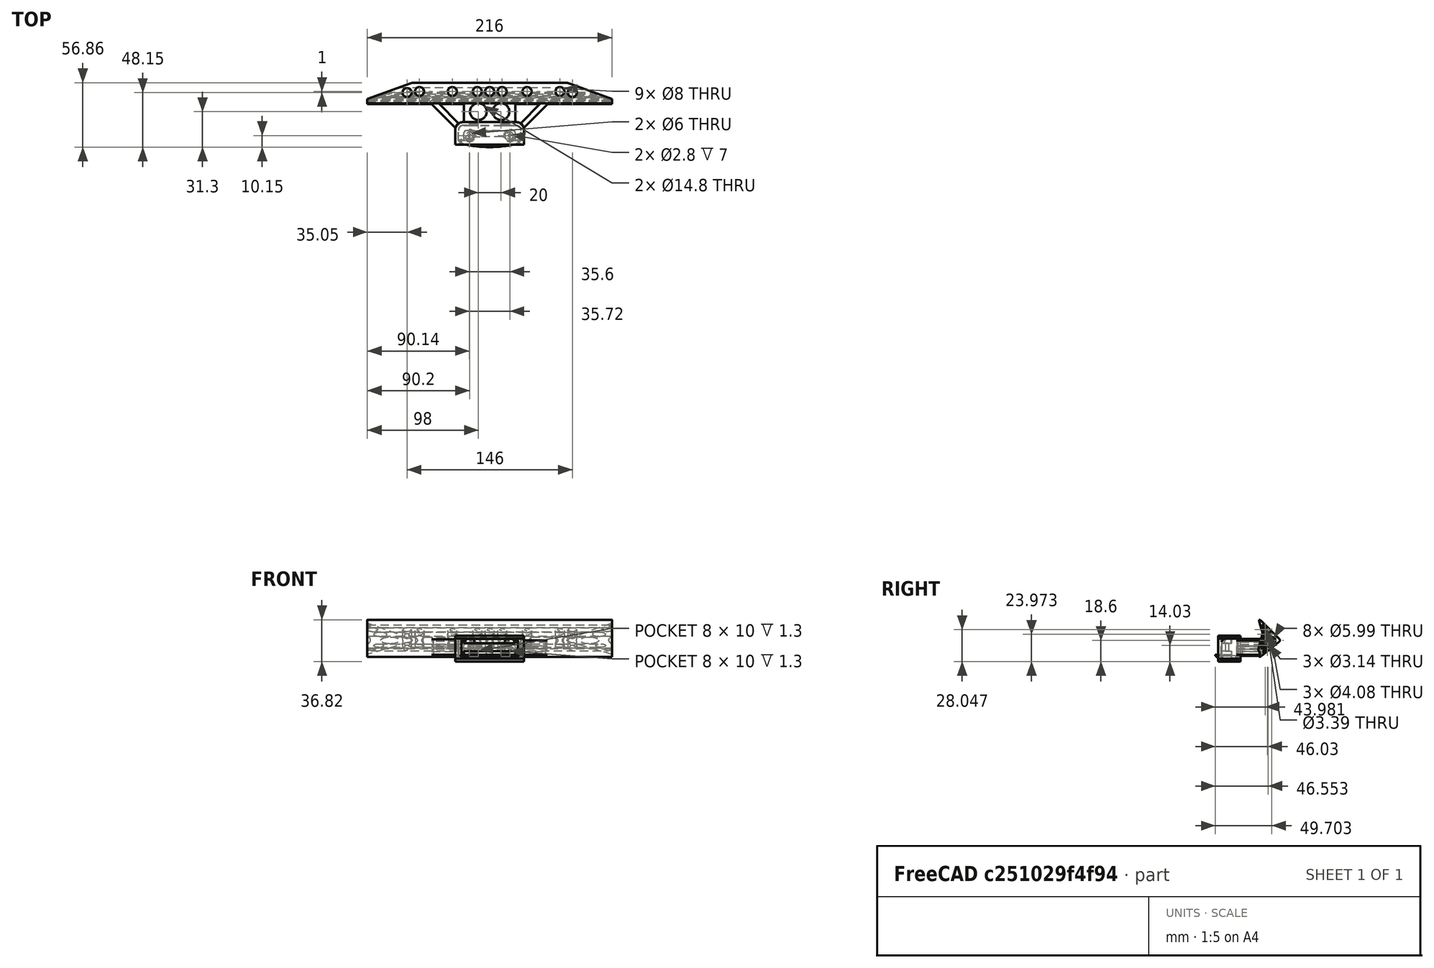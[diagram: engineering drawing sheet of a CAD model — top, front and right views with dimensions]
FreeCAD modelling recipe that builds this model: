
FCSTD DOCUMENT  (FreeCAD 0.21R0.20.1)
Label: 060
License: All rights reserved
LicenseURL: http://en.wikipedia.org/wiki/All_rights_reserved
objects: Part::Cylinder×29, Part::MultiFuse×16, Part::Extrusion×13, Sketcher::SketchObject×12, Part::Box×9, Part::Cut×8, Part::Fillet×8, Part::Chamfer×4
note: 99 computed .brp shape members not serialized (recipe doc carries the construction recipe); baked Part::Feature solids carry a one-line shape summary decoded from their .brp

FEATURE [Sketcher::SketchObject] Sketch  label="attatchmentPiece"
  FullyConstrained = true
  sketch-geometry (20):
    g0: LineSegment StartX=21.05 StartY=0 StartZ=0 EndX=21.05 EndY=-1 EndZ=0
    g1: LineSegment StartX=21.05 StartY=-1 StartZ=0 EndX=21.05 EndY=-4.3 EndZ=0
    g2: LineSegment StartX=-24.15 StartY=4.3 StartZ=0 EndX=21.05 EndY=4.3 EndZ=0
    g3: LineSegment StartX=21.05 StartY=0 StartZ=0 EndX=21.05 EndY=4.3 EndZ=0
    g4-g7: Circle x4 (B-spline internal-alignment scaffolding for g8; pole/knot coordinates omitted)
    g8: BSplineCurve PolesCount=4 KnotsCount=2 Degree=3 IsPeriodic=0
    g9: GeomPoint X=10.05 Y=-1 Z=0
    g10: GeomPoint X=14.55 Y=-4.3 Z=0
    g11: LineSegment StartX=10.05 StartY=-1 StartZ=0 EndX=-10.05 EndY=-1 EndZ=0
    g12: LineSegment StartX=14.55 StartY=-4.3 StartZ=0 EndX=21.05 EndY=-4.3 EndZ=0
    g13: LineSegment StartX=-24.15 StartY=4.3 StartZ=0 EndX=-24.15 EndY=-4.3 EndZ=0
    g14: LineSegment StartX=-13.15 StartY=-1 StartZ=0 EndX=-10.05 EndY=-1 EndZ=0
    g15: LineSegment StartX=-24.15 StartY=-4.3 StartZ=0 EndX=-19.35 EndY=-4.3 EndZ=0
    g16: LineSegment StartX=-19.35 StartY=-4.3 StartZ=0 EndX=-17.65 EndY=-4.3 EndZ=0
    g17: BSplineCurve PolesCount=4 KnotsCount=2 Degree=3 IsPeriodic=0
    g18: Circle CenterX=16.25 CenterY=0 CenterZ=0 NormalX=0 NormalY=0 NormalZ=1 AngleXU=0 Radius=1.4
    g19: Circle CenterX=-19.35 CenterY=0 CenterZ=0 NormalX=0 NormalY=0 NormalZ=1 AngleXU=0 Radius=1.4
  constraints (41):
    c: Vertical(g0)
    c: Coincident(g1,g0)
    c: Vertical(g1)
    c: Block(g0)
    c: Horizontal(g2)
    c: Vertical(g3)
    c: Coincident(g3,g2)
    c: Block(g2)
    c: Block(g3)
    c: Weight(g4) = 1
    c: Equal(g4,g5)
    c: Equal(g4,g6)
    c: Equal(g4,g7)
    c: InternalAlignment(g4-g7 -> g8) x4
    c: InternalAlignment(g9,g8)
    c: InternalAlignment(g10,g8)
    c: Block(g8)
    c: Coincident(g11,g8)
    c: Horizontal(g11)
    c: Coincident(g12,g8)
    c: Coincident(g12,g1)
    c: Horizontal(g12)
    c: Distance(g2) = 45.2
    c: Coincident(g13,g2)
    c: Vertical(g13)
    c: Horizontal(g14)
    c: Distance(g14) = 3.1
    c: Horizontal(g15)
    c: Block(g17)
    c: Coincident(g16,g15)
    c: Coincident(g16,g17)
    c: Horizontal(g16)
    c: Block(g16)
    c: Coincident(g17,g14)
    c: Block(g15)
    c: Block(g11)
    c: Block(g13)
    c: Distance(g15) = 4.8
    c: Distance(g16) = 1.7
    c: Block(g18)
    c: Block(g19)
FEATURE [Part::Extrusion] Extrude  label="attatchmentPiece001"
  Base = -> Sketch
  Dir = (0,0,1)
  DirMode = 2
  FaceMakerClass = Part::FaceMakerBullseye
  LengthFwd = 7
  LengthRev = 0
  Solid = true
  Symmetric = false
FEATURE [Sketcher::SketchObject] Sketch001  label="attatchmentPieceSurround"
  FullyConstrained = true
  sketch-geometry (18):
    g0: LineSegment StartX=25.85 StartY=-4.3 StartZ=0 EndX=21.05 EndY=-4.3 EndZ=0
    g1: LineSegment StartX=25.85 StartY=-4.3 StartZ=0 EndX=25.85 EndY=4.3 EndZ=0
    g2: LineSegment StartX=-21.05 StartY=8.9 StartZ=0 EndX=21.05 EndY=8.9 EndZ=0
    g3: Circle CenterX=21.05 CenterY=8.9 CenterZ=0 NormalX=0 NormalY=0 NormalZ=1 AngleXU=0 Radius=1
    g4: Circle CenterX=25.85 CenterY=8.9 CenterZ=0 NormalX=0 NormalY=0 NormalZ=1 AngleXU=0 Radius=1
    g5: Circle CenterX=25.85 CenterY=4.3 CenterZ=0 NormalX=0 NormalY=0 NormalZ=1 AngleXU=0 Radius=1
    g6: BSplineCurve PolesCount=3 KnotsCount=2 Degree=2 IsPeriodic=0
    g7: GeomPoint X=21.05 Y=8.9 Z=0
    g8: GeomPoint X=25.85 Y=4.3 Z=0
    g9: ArcOfCircle CenterX=19.45 CenterY=2.7 CenterZ=0 NormalX=0 NormalY=0 NormalZ=1 AngleXU=0 Radius=1.6 StartAngle=0 EndAngle=1.5708
    g10: LineSegment StartX=21.05 StartY=2.7 StartZ=0 EndX=21.05 EndY=-4.3 EndZ=0
    g11: BSplineCurve PolesCount=3 KnotsCount=2 Degree=2 IsPeriodic=0
    g12: LineSegment StartX=-28.95 StartY=-4.3 StartZ=0 EndX=-28.95 EndY=4.3 EndZ=0
    g13: LineSegment StartX=-24.15 StartY=-4.3 StartZ=0 EndX=-28.95 EndY=-4.3 EndZ=0
    g14: LineSegment StartX=-24.15 StartY=2.7 StartZ=0 EndX=-24.15 EndY=-4.3 EndZ=0
    g15: ArcOfCircle CenterX=-22.55 CenterY=2.7 CenterZ=0 NormalX=0 NormalY=0 NormalZ=1 AngleXU=0 Radius=1.6 StartAngle=1.5708 EndAngle=3.14159
    g16: LineSegment StartX=-24.15 StartY=8.9 StartZ=0 EndX=-21.05 EndY=8.9 EndZ=0
    g17: LineSegment StartX=-22.55 StartY=4.3 StartZ=0 EndX=19.45 EndY=4.3 EndZ=0
  constraints (38):
    c: Horizontal(g0)
    c: Vertical(g1)
    c: Coincident(g1,g0)
    c: Horizontal(g2)
    c: Distance(g2) = 42.1
    c: Block(g2)
    c: Coincident(g6,g2)
    c: Weight(g3) = 1
    c: Equal(g3,g4)
    c: Equal(g3,g5)
    c: Coincident(g6,g1)
    c: InternalAlignment(g3,g6)
    c: InternalAlignment(g4,g6)
    c: InternalAlignment(g5,g6)
    c: InternalAlignment(g7,g6)
    c: InternalAlignment(g8,g6)
    c: Block(g0)
    c: Block(g6)
    c: Block(g9)
    c: Coincident(g10,g9)
    c: Coincident(g10,g0)
    c: Vertical(g10)
    c: Horizontal(g13)
    c: Coincident(g12,g13)
    c: Vertical(g12)
    c: Coincident(g11,g12)
    c: Block(g12)
    c: Block(g11)
    c: Block(g15)
    c: Coincident(g14,g15)
    c: Coincident(g14,g13)
    c: Vertical(g14)
    c: Coincident(g16,g11)
    c: Coincident(g16,g2)
    c: Horizontal(g16)
    c: Coincident(g17,g15)
    c: Coincident(g17,g9)
    c: Horizontal(g17)
FEATURE [Part::Extrusion] Extrude001  label="attatchmentPieceSurround001"
  Base = -> Sketch001
  Dir = (0,0,1)
  DirMode = 2
  FaceMakerClass = Part::FaceMakerBullseye
  LengthFwd = 14.7
  LengthRev = 0
  Placement = pos=(0,0,-4.1) rot=(0,0,1;0rad)
  Solid = true
  Symmetric = false
FEATURE [Sketcher::SketchObject] Sketch002  label="attatchmentPieceEndScrewHoleCaps"
  FullyConstrained = true
  sketch-geometry (10):
    g0: ArcOfCircle CenterX=16.25 CenterY=0 CenterZ=0 NormalX=0 NormalY=0 NormalZ=1 AngleXU=0 Radius=4.3 StartAngle=2.05456 EndAngle=5.79942
    g1: LineSegment StartX=14.25 StartY=3.80657 StartZ=0 EndX=14.25 EndY=6 EndZ=0
    g2: LineSegment StartX=20.0566 StartY=-2 StartZ=0 EndX=22.25 EndY=-2 EndZ=0
    g3: LineSegment StartX=22.25 StartY=-2 StartZ=0 EndX=22.25 EndY=6 EndZ=0
    g4: LineSegment StartX=14.25 StartY=6 StartZ=0 EndX=22.25 EndY=6 EndZ=0
    g5: LineSegment StartX=-25.35 StartY=-2 StartZ=0 EndX=-25.35 EndY=6 EndZ=0
    g6: LineSegment StartX=-25.35 StartY=-2 StartZ=0 EndX=-23.1566 EndY=-2 EndZ=0
    g7: LineSegment StartX=-17.35 StartY=6 StartZ=0 EndX=-25.35 EndY=6 EndZ=0
    g8: LineSegment StartX=-17.35 StartY=3.80657 StartZ=0 EndX=-17.35 EndY=6 EndZ=0
    g9: ArcOfCircle CenterX=-19.35 CenterY=0 CenterZ=0 NormalX=0 NormalY=0 NormalZ=1 AngleXU=0 Radius=4.3 StartAngle=3.62536 EndAngle=7.37022
  constraints (25):
    c: Block(g0)
    c: Vertical(g1)
    c: Horizontal(g2)
    c: Coincident(g3,g2)
    c: Vertical(g3)
    c: Coincident(g4,g1)
    c: Horizontal(g4)
    c: Coincident(g3,g4)
    c: Block(g4)
    c: Block(g3)
    c: Coincident(g0,g1)
    c: Coincident(g0,g2)
    c: Block(g1)
    c: Block(g9)
    c: Horizontal(g6)
    c: Vertical(g8)
    c: Coincident(g7,g8)
    c: Horizontal(g7)
    c: Coincident(g5,g6)
    c: Vertical(g5)
    c: Coincident(g5,g7)
    c: Block(g7)
    c: Block(g5)
    c: Coincident(g9,g6)
    c: Coincident(g9,g8)
FEATURE [Part::Extrusion] Extrude002  label="attatchmentPieceEndScrewHoleCaps001"
  Base = -> Sketch002
  Dir = (0,0,1)
  DirMode = 2
  FaceMakerClass = Part::FaceMakerBullseye
  LengthFwd = 3.6
  LengthRev = 0
  Placement = pos=(0,0,7) rot=(0,0,1;0rad)
  Solid = true
  Symmetric = false
FEATURE [Sketcher::SketchObject] Sketch003  label="mainBumpperPieceAttatchment"
  FullyConstrained = true
  sketch-geometry (42):
    g0: Circle CenterX=28.85 CenterY=4.3 CenterZ=0 NormalX=0 NormalY=0 NormalZ=1 AngleXU=0 Radius=1
    g1: Circle CenterX=28.85 CenterY=11.9 CenterZ=0 NormalX=0 NormalY=0 NormalZ=1 AngleXU=0 Radius=1
    g2: Circle CenterX=21.05 CenterY=11.9 CenterZ=0 NormalX=0 NormalY=0 NormalZ=1 AngleXU=0 Radius=1
    g3: BSplineCurve PolesCount=3 KnotsCount=2 Degree=2 IsPeriodic=0
    g4: GeomPoint X=28.85 Y=4.3 Z=0
    g5: GeomPoint X=21.05 Y=11.9 Z=0
    g6: LineSegment StartX=-21.05 StartY=11.9 StartZ=0 EndX=21.05 EndY=11.9 EndZ=0
    g7: LineSegment StartX=28.85 StartY=4.3 StartZ=0 EndX=28.85 EndY=-4.3 EndZ=0
    g8: Circle CenterX=21.05 CenterY=9.2 CenterZ=0 NormalX=0 NormalY=0 NormalZ=1 AngleXU=0 Radius=1
    g9: Circle CenterX=26.15 CenterY=9.2 CenterZ=0 NormalX=0 NormalY=0 NormalZ=1 AngleXU=0 Radius=1
    g10: Circle CenterX=26.15 CenterY=4.3 CenterZ=0 NormalX=0 NormalY=0 NormalZ=1 AngleXU=0 Radius=1
    g11: BSplineCurve PolesCount=3 KnotsCount=2 Degree=2 IsPeriodic=0
    g12: GeomPoint X=21.05 Y=9.2 Z=0
    g13: GeomPoint X=26.15 Y=4.3 Z=0
    g14: LineSegment StartX=-21.05 StartY=9.2 StartZ=0 EndX=21.05 EndY=9.2 EndZ=0
    g15: LineSegment StartX=26.15 StartY=-4.3 StartZ=0 EndX=26.15 EndY=4.3 EndZ=0
    g16: LineSegment StartX=26.15 StartY=-4.3 StartZ=0 EndX=26.15 EndY=-4.6 EndZ=0
    g17: LineSegment StartX=23.45 StartY=-4.6 StartZ=0 EndX=26.15 EndY=-4.6 EndZ=0
    g18: LineSegment StartX=28.85 StartY=-4.3 StartZ=0 EndX=28.85 EndY=-7.9 EndZ=0
    g19: LineSegment StartX=23.45 StartY=-4.6 StartZ=0 EndX=23.45 EndY=-5.3 EndZ=0
    g20: Circle CenterX=28.85 CenterY=-7.9 CenterZ=0 NormalX=0 NormalY=0 NormalZ=1 AngleXU=0 Radius=1
    g21: Circle CenterX=26.15 CenterY=-8.2 CenterZ=0 NormalX=0 NormalY=0 NormalZ=1 AngleXU=0 Radius=1
    g22: Circle CenterX=23.45 CenterY=-5.3 CenterZ=0 NormalX=0 NormalY=0 NormalZ=1 AngleXU=0 Radius=1
    g23: BSplineCurve PolesCount=3 KnotsCount=2 Degree=2 IsPeriodic=0
    g24: GeomPoint X=28.85 Y=-7.9 Z=0
    g25: GeomPoint X=23.45 Y=-5.3 Z=0
    g26: LineSegment StartX=-21.05 StartY=9.2 StartZ=0 EndX=-24.15 EndY=9.2 EndZ=0
    g27: BSplineCurve PolesCount=3 KnotsCount=2 Degree=2 IsPeriodic=0
    g28: LineSegment StartX=-29.25 StartY=-4.3 StartZ=0 EndX=-29.25 EndY=-4.6 EndZ=0
    g29: LineSegment StartX=-29.25 StartY=-4.6 StartZ=0 EndX=-26.55 EndY=-4.6 EndZ=0
    g30: LineSegment StartX=-31.95 StartY=-4.3 StartZ=0 EndX=-31.95 EndY=-7.9 EndZ=0
    g31: LineSegment StartX=-26.55 StartY=-4.6 StartZ=0 EndX=-26.55 EndY=-5.3 EndZ=0
    g32: Circle CenterX=-31.95 CenterY=-7.9 CenterZ=0 NormalX=0 NormalY=0 NormalZ=1 AngleXU=0 Radius=1
    g33: Circle CenterX=-29.25 CenterY=-8.2 CenterZ=0 NormalX=0 NormalY=0 NormalZ=1 AngleXU=0 Radius=1
    g34: Circle CenterX=-26.55 CenterY=-5.3 CenterZ=0 NormalX=0 NormalY=0 NormalZ=1 AngleXU=0 Radius=1
    g35: BSplineCurve PolesCount=3 KnotsCount=2 Degree=2 IsPeriodic=0
    g36: GeomPoint X=-31.95 Y=-7.9 Z=0
    g37: GeomPoint X=-26.55 Y=-5.3 Z=0
    g38: LineSegment StartX=-31.95 StartY=4.3 StartZ=0 EndX=-31.95 EndY=-4.3 EndZ=0
    g39: LineSegment StartX=-29.25 StartY=-4.3 StartZ=0 EndX=-29.25 EndY=4.3 EndZ=0
    g40: BSplineCurve PolesCount=3 KnotsCount=2 Degree=2 IsPeriodic=0
    g41: LineSegment StartX=-21.05 StartY=11.9 StartZ=0 EndX=-24.15 EndY=11.9 EndZ=0
  constraints (78):
    c: Weight(g0) = 1
    c: Equal(g0,g1)
    c: Equal(g0,g2)
    c: InternalAlignment(g0,g3)
    c: InternalAlignment(g1,g3)
    c: InternalAlignment(g2,g3)
    c: InternalAlignment(g4,g3)
    c: InternalAlignment(g5,g3)
    c: Block(g3)
    c: Horizontal(g6)
    c: Vertical(g7)
    c: Block(g7)
    c: Block(g6)
    c: Weight(g8) = 1
    c: Equal(g8,g9)
    c: Equal(g8,g10)
    c: InternalAlignment(g8,g11)
    c: InternalAlignment(g9,g11)
    c: InternalAlignment(g10,g11)
    c: InternalAlignment(g12,g11)
    c: InternalAlignment(g13,g11)
    c: Horizontal(g14)
    c: Vertical(g15)
    c: Block(g11)
    c: Block(g15)
    c: Block(g14)
    c: Coincident(g16,g15)
    c: Vertical(g16)
    c: Distance(g16) = 0.3
    c: Horizontal(g17)
    c: Coincident(g17,g16)
    c: Coincident(g18,g7)
    c: Vertical(g18)
    c: Distance(g18) = 3.6
    c: Vertical(g19)
    c: Coincident(g19,g17)
    c: Coincident(g23,g18)
    c: Weight(g20) = 1
    c: Equal(g20,g21)
    c: Equal(g20,g22)
    c: Coincident(g23,g19)
    c: InternalAlignment(g20,g23)
    c: InternalAlignment(g21,g23)
    c: InternalAlignment(g22,g23)
    c: InternalAlignment(g24,g23)
    c: InternalAlignment(g25,g23)
    c: Block(g23)
    c: Horizontal(g26)
    c: Distance(g26) = 3.1
    c: Block(g27)
    c: Vertical(g38)
    c: Block(g38)
    c: Vertical(g39)
    c: Block(g40)
    c: Block(g39)
    c: Vertical(g28)
    c: Coincident(g28,g39)
    c: Coincident(g29,g28)
    c: Horizontal(g29)
    c: Vertical(g30)
    c: Coincident(g30,g38)
    c: Coincident(g31,g29)
    c: Vertical(g31)
    c: Coincident(g35,g30)
    c: Equal(g32,g33)
    c: Equal(g32,g34)
    c: Coincident(g35,g31)
    c: InternalAlignment(g32,g35)
    c: InternalAlignment(g33,g35)
    c: InternalAlignment(g34,g35)
    c: InternalAlignment(g36,g35)
    c: InternalAlignment(g37,g35)
    c: Block(g35)
    c: Coincident(g40,g26)
    c: Block(g29)
    c: Horizontal(g41)
    c: Equal(g26,g41) = 3.1
    c: Coincident(g41,g6)
FEATURE [Part::Box] Box  label="bumpperExtension"
  AttacherType = Attacher::AttachEngine3D
  Height = 14.7
  Length = 45.2
  Placement = pos=(-24.15,11.9,-4.1) rot=(0,0,1;0rad)
  Width = 18
FEATURE [Sketcher::SketchObject] Sketch004  label="bumpperMain"
  FullyConstrained = true
  Placement = pos=(0,0,0) rot=(0.57735,0.57735,0.57735;2.0944rad)
  sketch-geometry (62):
    g0: Circle CenterX=-3.12329 CenterY=2.49901 CenterZ=0 NormalX=0 NormalY=0 NormalZ=1 AngleXU=0 Radius=1
    g1: Circle CenterX=0 CenterY=0 CenterZ=0 NormalX=0 NormalY=0 NormalZ=1 AngleXU=0 Radius=1
    g2: Circle CenterX=-1.35243 CenterY=3.60648 CenterZ=0 NormalX=0 NormalY=0 NormalZ=1 AngleXU=0 Radius=1
    g3: BSplineCurve PolesCount=3 KnotsCount=2 Degree=2 IsPeriodic=0
    g4: GeomPoint X=-3.12329 Y=2.49901 Z=0
    g5: GeomPoint X=-1.35243 Y=3.60648 Z=0
    g6: Circle CenterX=-2.83953 CenterY=33.0261 CenterZ=0 NormalX=0 NormalY=0 NormalZ=1 AngleXU=0 Radius=1
    g7: Circle CenterX=0 CenterY=35.8434 CenterZ=0 NormalX=0 NormalY=0 NormalZ=1 AngleXU=0 Radius=1
    g8: Circle CenterX=-1.15771 CenterY=32.0146 CenterZ=0 NormalX=0 NormalY=0 NormalZ=1 AngleXU=0 Radius=1
    g9: BSplineCurve PolesCount=3 KnotsCount=2 Degree=2 IsPeriodic=0
    g10: GeomPoint X=-2.83953 Y=33.0261 Z=0
    g11: GeomPoint X=-1.15771 Y=32.0146 Z=0
    g12: Circle CenterX=-18.2963 CenterY=17.6904 CenterZ=0 NormalX=0 NormalY=0 NormalZ=1 AngleXU=0 Radius=1
    g13: Circle CenterX=-20 CenterY=16 CenterZ=0 NormalX=0 NormalY=0 NormalZ=1 AngleXU=0 Radius=1
    g14: Circle CenterX=-18.1259 CenterY=14.5008 CenterZ=0 NormalX=0 NormalY=0 NormalZ=1 AngleXU=0 Radius=1
    g15: BSplineCurve PolesCount=3 KnotsCount=2 Degree=2 IsPeriodic=0
    g16: GeomPoint X=-18.2963 Y=17.6904 Z=0
    g17: GeomPoint X=-18.1259 Y=14.5008 Z=0
    g18: LineSegment StartX=-18.2963 StartY=17.6904 StartZ=0 EndX=-2.83953 EndY=33.0261 EndZ=0
    g19: LineSegment StartX=-18.1259 StartY=14.5008 StartZ=0 EndX=-3.12329 EndY=2.49901 EndZ=0
    g20: Circle CenterX=-11.9527 CenterY=16 CenterZ=0 NormalX=0 NormalY=0 NormalZ=1 AngleXU=0 Radius=2.99582
    g21: Circle CenterX=-8.803 CenterY=21.3731 CenterZ=0 NormalX=0 NormalY=0 NormalZ=1 AngleXU=0 Radius=2.03939
    g22: Circle CenterX=-6.23123 CenterY=25.4475 CenterZ=0 NormalX=0 NormalY=0 NormalZ=1 AngleXU=0 Radius=1.69309
    g23: Circle CenterX=-4.38186 CenterY=28.6261 CenterZ=0 NormalX=0 NormalY=0 NormalZ=1 AngleXU=0 Radius=1.13029
    g24: Circle CenterX=-8.28033 CenterY=11.4296 CenterZ=0 NormalX=0 NormalY=0 NormalZ=1 AngleXU=0 Radius=1.57213
    g25: Circle CenterX=-5.93972 CenterY=8.22213 CenterZ=0 NormalX=0 NormalY=0 NormalZ=1 AngleXU=0 Radius=1.28743
    g26: Circle CenterX=-3.47023 CenterY=24.3665 CenterZ=0 NormalX=0 NormalY=0 NormalZ=1 AngleXU=0 Radius=1
    g27: Circle CenterX=-3.90437 CenterY=22.9307 CenterZ=0 NormalX=0 NormalY=0 NormalZ=1 AngleXU=0 Radius=1
    g28: Circle CenterX=-3.53772 CenterY=21.4762 CenterZ=0 NormalX=0 NormalY=0 NormalZ=1 AngleXU=0 Radius=1
    g29: BSplineCurve PolesCount=3 KnotsCount=2 Degree=2 IsPeriodic=0
    g30: GeomPoint X=-3.47023 Y=24.3665 Z=0
    g31: GeomPoint X=-3.53772 Y=21.4762 Z=0
    g32: LineSegment StartX=-1.15771 StartY=32.0146 StartZ=0 EndX=-3.47023 EndY=24.3665 EndZ=0
    g33: Circle CenterX=-5.41867 CenterY=17.9226 CenterZ=0 NormalX=0 NormalY=0 NormalZ=1 AngleXU=0 Radius=1
    g34: Circle CenterX=-6 CenterY=16 CenterZ=0 NormalX=0 NormalY=0 NormalZ=1 AngleXU=0 Radius=1
    g35: Circle CenterX=-5.22753 CenterY=13.9401 CenterZ=0 NormalX=0 NormalY=0 NormalZ=1 AngleXU=0 Radius=1
    g36: BSplineCurve PolesCount=3 KnotsCount=2 Degree=2 IsPeriodic=0
    g37: GeomPoint X=-5.41867 Y=17.9226 Z=0
    g38: GeomPoint X=-5.22753 Y=13.9401 Z=0
    g39: Circle CenterX=-3.98946 CenterY=10.6386 CenterZ=0 NormalX=0 NormalY=0 NormalZ=1 AngleXU=0 Radius=1
    g40: Circle CenterX=-2.58497 CenterY=6.89324 CenterZ=0 NormalX=0 NormalY=0 NormalZ=1 AngleXU=0 Radius=1
    g41: Circle CenterX=-3.11001 CenterY=10.8586 CenterZ=0 NormalX=0 NormalY=0 NormalZ=1 AngleXU=0 Radius=1
    g42: BSplineCurve PolesCount=3 KnotsCount=2 Degree=2 IsPeriodic=0
    g43: GeomPoint X=-3.98946 Y=10.6386 Z=0
    g44: GeomPoint X=-3.11001 Y=10.8586 Z=0
    g45: Circle CenterX=-1.35243 CenterY=3.60648 CenterZ=0 NormalX=0 NormalY=0 NormalZ=1 AngleXU=0 Radius=1
    g46: Circle CenterX=-1.76142 CenterY=4.69712 CenterZ=0 NormalX=0 NormalY=0 NormalZ=1 AngleXU=0 Radius=1
    g47: Circle CenterX=-1.05937 CenterY=5.79125 CenterZ=0 NormalX=0 NormalY=0 NormalZ=1 AngleXU=0 Radius=1
    g48: BSplineCurve PolesCount=3 KnotsCount=2 Degree=2 IsPeriodic=0
    g49: GeomPoint X=-1.35243 Y=3.60648 Z=0
    g50: GeomPoint X=-1.05937 Y=5.79125 Z=0
    g51: Circle CenterX=-0.519336 CenterY=6.6329 CenterZ=0 NormalX=0 NormalY=0 NormalZ=1 AngleXU=0 Radius=1
    g52: Circle CenterX=0 CenterY=7.44228 CenterZ=0 NormalX=0 NormalY=0 NormalZ=1 AngleXU=0 Radius=1
    g53: Circle CenterX=-0.244436 CenterY=8.41194 CenterZ=0 NormalX=0 NormalY=0 NormalZ=1 AngleXU=0 Radius=1
    g54: BSplineCurve PolesCount=3 KnotsCount=2 Degree=2 IsPeriodic=0
    g55: GeomPoint X=-0.519336 Y=6.6329 Z=0
    g56: GeomPoint X=-0.244436 Y=8.41194 Z=0
    g57: LineSegment StartX=-3.53772 StartY=21.4762 StartZ=0 EndX=-0.244436 EndY=8.41194 EndZ=0
    g58: LineSegment StartX=-5.22753 StartY=13.9401 StartZ=0 EndX=-3.98946 EndY=10.6386 EndZ=0
    g59: LineSegment StartX=-1.05937 StartY=5.79125 StartZ=0 EndX=-0.519336 EndY=6.6329 EndZ=0
    g60: BSplineCurve PolesCount=3 KnotsCount=2 Degree=2 IsPeriodic=0
    g61: LineSegment StartX=-4.0304 StartY=17.8099 StartZ=0 EndX=-3.11001 EndY=10.8586 EndZ=0
  constraints (96):
    c: Weight(g0) = 1
    c: Equal(g0,g1)
    c: Equal(g0,g2)
    c: InternalAlignment(g0,g3)
    c: InternalAlignment(g1,g3)
    c: InternalAlignment(g2,g3)
    c: InternalAlignment(g4,g3)
    c: InternalAlignment(g5,g3)
    c: Block(g3)
    c: Weight(g6) = 1
    c: Equal(g6,g7)
    c: Equal(g6,g8)
    c: InternalAlignment(g6,g9)
    c: InternalAlignment(g7,g9)
    c: InternalAlignment(g8,g9)
    c: InternalAlignment(g10,g9)
    c: InternalAlignment(g11,g9)
    c: Block(g9)
    c: Weight(g12) = 1
    c: Equal(g12,g13)
    c: Equal(g12,g14)
    c: InternalAlignment(g12,g15)
    c: InternalAlignment(g13,g15)
    c: InternalAlignment(g14,g15)
    c: InternalAlignment(g16,g15)
    c: InternalAlignment(g17,g15)
    c: Block(g15)
    c: Coincident(g18,g15)
    c: Coincident(g18,g9)
    c: Coincident(g19,g15)
    c: Coincident(g19,g3)
    c: Block(g25)
    c: Block(g24)
    c: Block(g20)
    c: Block(g21)
    c: Block(g22)
    c: Block(g23)
    c: Weight(g26) = 1
    c: Equal(g26,g27)
    c: Equal(g26,g28)
    c: InternalAlignment(g26,g29)
    c: InternalAlignment(g27,g29)
    c: InternalAlignment(g28,g29)
    c: InternalAlignment(g30,g29)
    c: InternalAlignment(g31,g29)
    c: Block(g29)
    c: Coincident(g32,g9)
    c: Coincident(g32,g29)
    c: Weight(g33) = 1
    c: Equal(g33,g34)
    c: Equal(g33,g35)
    c: InternalAlignment(g33,g36)
    c: InternalAlignment(g34,g36)
    c: InternalAlignment(g35,g36)
    c: InternalAlignment(g37,g36)
    c: InternalAlignment(g38,g36)
    c: Block(g36)
    c: Weight(g39) = 1
    c: Equal(g39,g40)
    c: Equal(g39,g41)
    c: InternalAlignment(g39,g42)
    c: InternalAlignment(g40,g42)
    c: InternalAlignment(g41,g42)
    c: InternalAlignment(g43,g42)
    c: InternalAlignment(g44,g42)
    c: Block(g42)
    c: Coincident(g48,g3)
    c: Weight(g45) = 1
    c: Equal(g45,g46)
    c: Equal(g45,g47)
    c: InternalAlignment(g45,g48)
    c: InternalAlignment(g46,g48)
    c: InternalAlignment(g47,g48)
    c: InternalAlignment(g49,g48)
    c: InternalAlignment(g50,g48)
    c: Block(g48)
    c: Weight(g51) = 1
    c: Equal(g51,g52)
    c: Equal(g51,g53)
    c: InternalAlignment(g51,g54)
    c: InternalAlignment(g52,g54)
    c: InternalAlignment(g53,g54)
    c: InternalAlignment(g55,g54)
    c: InternalAlignment(g56,g54)
    c: Block(g54)
    c: Coincident(g57,g29)
    c: Coincident(g57,g54)
    c: Block(g57)
    c: Coincident(g58,g36)
    c: Coincident(g58,g42)
    c: Coincident(g59,g48)
    c: Coincident(g59,g54)
    c: Block(g60)
    c: Coincident(g60,g36)
    c: Coincident(g61,g60)
    c: Coincident(g61,g42)
FEATURE [Part::Extrusion] Extrude004  label="bumpperMain001"
  Base = -> Sketch004
  Dir = (1,0,0)
  DirMode = 2
  FaceMakerClass = Part::FaceMakerBullseye
  LengthFwd = 216
  LengthRev = 0
  Placement = pos=(106.45,27.6,-6.6) rot=(0,0,1;3.14159rad)
  Solid = true
  Symmetric = false
FEATURE [Sketcher::SketchObject] Sketch005  label="attatchmentPieceBottom"
  FullyConstrained = true
  sketch-geometry (20):
    g0: LineSegment StartX=25.85 StartY=-4.3 StartZ=0 EndX=25.85 EndY=4.3 EndZ=0
    g1: LineSegment StartX=-21.05 StartY=8.9 StartZ=0 EndX=21.05 EndY=8.9 EndZ=0
    g2: Circle CenterX=21.05 CenterY=8.9 CenterZ=0 NormalX=0 NormalY=0 NormalZ=1 AngleXU=0 Radius=1
    g3: Circle CenterX=25.85 CenterY=8.9 CenterZ=0 NormalX=0 NormalY=0 NormalZ=1 AngleXU=0 Radius=1
    g4: Circle CenterX=25.85 CenterY=4.3 CenterZ=0 NormalX=0 NormalY=0 NormalZ=1 AngleXU=0 Radius=1
    g5: BSplineCurve PolesCount=3 KnotsCount=2 Degree=2 IsPeriodic=0
    g6: GeomPoint X=21.05 Y=8.9 Z=0
    g7: GeomPoint X=25.85 Y=4.3 Z=0
    g8: BSplineCurve PolesCount=3 KnotsCount=2 Degree=2 IsPeriodic=0
    g9: LineSegment StartX=-28.95 StartY=-4.3 StartZ=0 EndX=-28.95 EndY=4.3 EndZ=0
    g10: LineSegment StartX=-24.15 StartY=8.9 StartZ=0 EndX=-21.05 EndY=8.9 EndZ=0
    g11: Circle CenterX=-19.41 CenterY=0 CenterZ=0 NormalX=0 NormalY=0 NormalZ=1 AngleXU=0 Radius=3
    g12: Circle CenterX=16.3103 CenterY=0 CenterZ=0 NormalX=0 NormalY=0 NormalZ=1 AngleXU=0 Radius=3
    g13-g16: Circle x4 (B-spline internal-alignment scaffolding for g17; pole/knot coordinates omitted)
    g17: BSplineCurve PolesCount=4 KnotsCount=2 Degree=3 IsPeriodic=0
    g18: GeomPoint X=-28.95 Y=-4.3 Z=0
    g19: GeomPoint X=25.85 Y=-4.3 Z=0
  constraints (36):
    c: Vertical(g0)
    c: Horizontal(g1)
    c: Distance(g1) = 42.1
    c: Block(g1)
    c: Coincident(g5,g1)
    c: Weight(g2) = 1
    c: Equal(g2,g3)
    c: Equal(g2,g4)
    c: Coincident(g5,g0)
    c: InternalAlignment(g2,g5)
    c: InternalAlignment(g3,g5)
    c: InternalAlignment(g4,g5)
    c: InternalAlignment(g6,g5)
    c: InternalAlignment(g7,g5)
    c: Block(g5)
    c: Vertical(g9)
    c: Coincident(g8,g9)
    c: Block(g9)
    c: Block(g8)
    c: Coincident(g10,g8)
    c: Coincident(g10,g1)
    c: Horizontal(g10)
    c: PointOnObject(g12,g-1)
    c: PointOnObject(g11,g-1)
    c: Block(g11)
    c: Block(g12)
    c: Coincident(g17,g9)
    c: Weight(g13) = 1
    c: Equal(g13,g14)
    c: Equal(g13,g15)
    c: Equal(g13,g16)
    c: Coincident(g17,g0)
    c: InternalAlignment(g13-g16 -> g17) x4
    c: InternalAlignment(g18,g17)
    c: InternalAlignment(g19,g17)
    c: Block(g17)
FEATURE [Part::Extrusion] Extrude005  label="removeFromMainBumpperPieceAttatchment"
  Base = -> Sketch005
  Dir = (0,0,1)
  DirMode = 2
  FaceMakerClass = Part::FaceMakerBullseye
  LengthFwd = 3.2
  LengthRev = 0
  Placement = pos=(0,0,-6.2) rot=(0,0,1;0rad)
  Solid = true
  Symmetric = false
FEATURE [Part::Extrusion] Extrude006  label="mainBumpperPieceAttatchment001"
  Base = -> Sketch003
  Dir = (0,0,1)
  DirMode = 2
  FaceMakerClass = Part::FaceMakerBullseye
  LengthFwd = 18.7
  LengthRev = 0
  Placement = pos=(0,0,-4.1) rot=(0,0,1;0rad)
  Solid = true
  Symmetric = false
FEATURE [Part::Cylinder] Cylinder  label="removeFromBumpperExtension"
  Angle = 360
  AttacherType = Attacher::AttachEngine3D
  FirstAngle = 0
  Height = 20
  Placement = pos=(8.45,21.15,-8) rot=(0,0,1;0rad)
  Radius = 7.4
  SecondAngle = 0
FEATURE [Part::Cylinder] Cylinder001  label="removeFromBumpperExtension001"
  Angle = 360
  AttacherType = Attacher::AttachEngine3D
  FirstAngle = 0
  Height = 20
  Placement = pos=(-11.55,21.15,-8) rot=(0,0,1;0rad)
  Radius = 7.4
  SecondAngle = 0
FEATURE [Part::MultiFuse] Fusion  label="removeFromBumpperExtension002"
  Shapes = -> [Cylinder,Cylinder001]
FEATURE [Part::Cylinder] Cylinder002  label="removeFromBumpperExtension004"
  Angle = 360
  AttacherType = Attacher::AttachEngine3D
  FirstAngle = 0
  Height = 20
  Placement = pos=(8.45,21.15,-8) rot=(0,0,1;0rad)
  Radius = 7.4
  SecondAngle = 0
FEATURE [Part::Cylinder] Cylinder003  label="removeFromBumpperExtension005"
  Angle = 360
  AttacherType = Attacher::AttachEngine3D
  FirstAngle = 0
  Height = 20
  Placement = pos=(-11.55,21.15,-8) rot=(0,0,1;0rad)
  Radius = 7.4
  SecondAngle = 0
FEATURE [Part::MultiFuse] Fusion001  label="removeFromBumpperMain"
  Shapes = -> [Cylinder002,Cylinder003]
FEATURE [Part::Cut] Cut  label="bumpperExtension001"
  Base = -> Box
  Tool = -> Fusion
FEATURE [Part::Fillet] Fillet  label="bumpperExtension002"
  Base = -> Cut
  Edges = 4 edges r=3: [Edge2,Edge4,Edge9,Edge14]
FEATURE [Part::Box] Box001  label="bumpperExtensionBumpHole"
  AttacherType = Attacher::AttachEngine3D
  Height = 10
  Length = 8
  Placement = pos=(8.45,9.2,-1.8) rot=(0,0,1;0rad)
  Width = 1.3
FEATURE [Part::Box] Box002  label="bumpperExtensionBumpHole001"
  AttacherType = Attacher::AttachEngine3D
  Height = 10
  Length = 8
  Placement = pos=(-19.55,9.2,-1.8) rot=(0,0,1;0rad)
  Width = 1.3
FEATURE [Part::Box] Box003  label="attatchmentPieceSurroundBump"
  AttacherType = Attacher::AttachEngine3D
  Height = 9.2
  Length = 7.2
  Placement = pos=(8.85,8.9,-1.4) rot=(0,0,1;0rad)
  Width = 1.3
FEATURE [Part::Box] Box004  label="attatchmentPieceSurroundBump001"
  AttacherType = Attacher::AttachEngine3D
  Height = 9.2
  Length = 7.2
  Placement = pos=(-19.15,8.9,-1.4) rot=(0,0,1;0rad)
  Width = 1.3
FEATURE [Part::MultiFuse] Fusion002  label="attatchmentPieceSurroundBump002"
  Placement = pos=(0,-0.4,0) rot=(0,0,1;0rad)
  Shapes = -> [Box004,Box003]
FEATURE [Part::MultiFuse] Fusion003  label="bumpperExtensionBumpHole002"
  Shapes = -> [Box002,Box001]
FEATURE [Part::Cut] Cut002  label="mainBumpperPieceAttatchment002"
  Base = -> Extrude006
  Tool = -> Fusion003
FEATURE [Part::Fillet] Fillet003  label="attatchmentPieceEndScrewHoleCaps002"
  Base = -> Extrude002
  Edges = 6 edges r=2.4: [Edge4,Edge7,Edge15,Edge25,Edge28,Edge30]
FEATURE [Part::Fillet] Fillet004  label="attatchmentPieceSurround002"
  Base = -> Extrude001
  Edges = 3 edges r=1.2: [Edge19,Edge25,Edge31]
FEATURE [Part::Fillet] Fillet006  label="mainBumpperPieceAttatchment003"
  Base = -> Cut002
  Edges = 2 edges r=1.6: [Edge2,Edge55]
FEATURE [Sketcher::SketchObject] Sketch006  label="attatchmentPieceBottom002"
  FullyConstrained = true
  sketch-geometry (20):
    g0: LineSegment StartX=25.85 StartY=-4.3 StartZ=0 EndX=25.85 EndY=4.3 EndZ=0
    g1: LineSegment StartX=-21.05 StartY=8.9 StartZ=0 EndX=21.05 EndY=8.9 EndZ=0
    g2: Circle CenterX=21.05 CenterY=8.9 CenterZ=0 NormalX=0 NormalY=0 NormalZ=1 AngleXU=0 Radius=1
    g3: Circle CenterX=25.85 CenterY=8.9 CenterZ=0 NormalX=0 NormalY=0 NormalZ=1 AngleXU=0 Radius=1
    g4: Circle CenterX=25.85 CenterY=4.3 CenterZ=0 NormalX=0 NormalY=0 NormalZ=1 AngleXU=0 Radius=1
    g5: BSplineCurve PolesCount=3 KnotsCount=2 Degree=2 IsPeriodic=0
    g6: GeomPoint X=21.05 Y=8.9 Z=0
    g7: GeomPoint X=25.85 Y=4.3 Z=0
    g8: BSplineCurve PolesCount=3 KnotsCount=2 Degree=2 IsPeriodic=0
    g9: LineSegment StartX=-28.95 StartY=-4.3 StartZ=0 EndX=-28.95 EndY=4.3 EndZ=0
    g10: LineSegment StartX=-24.15 StartY=8.9 StartZ=0 EndX=-21.05 EndY=8.9 EndZ=0
    g11: Circle CenterX=-19.41 CenterY=0 CenterZ=0 NormalX=0 NormalY=0 NormalZ=1 AngleXU=0 Radius=3
    g12: Circle CenterX=16.3103 CenterY=0 CenterZ=0 NormalX=0 NormalY=0 NormalZ=1 AngleXU=0 Radius=3
    g13-g16: Circle x4 (B-spline internal-alignment scaffolding for g17; pole/knot coordinates omitted)
    g17: BSplineCurve PolesCount=4 KnotsCount=2 Degree=3 IsPeriodic=0
    g18: GeomPoint X=-28.95 Y=-4.3 Z=0
    g19: GeomPoint X=25.85 Y=-4.3 Z=0
  constraints (36):
    c: Vertical(g0)
    c: Horizontal(g1)
    c: Distance(g1) = 42.1
    c: Block(g1)
    c: Coincident(g5,g1)
    c: Weight(g2) = 1
    c: Equal(g2,g3)
    c: Equal(g2,g4)
    c: Coincident(g5,g0)
    c: InternalAlignment(g2,g5)
    c: InternalAlignment(g3,g5)
    c: InternalAlignment(g4,g5)
    c: InternalAlignment(g6,g5)
    c: InternalAlignment(g7,g5)
    c: Block(g5)
    c: Vertical(g9)
    c: Coincident(g8,g9)
    c: Block(g9)
    c: Block(g8)
    c: Coincident(g10,g8)
    c: Coincident(g10,g1)
    c: Horizontal(g10)
    c: PointOnObject(g12,g-1)
    c: PointOnObject(g11,g-1)
    c: Block(g11)
    c: Block(g12)
    c: Coincident(g17,g9)
    c: Weight(g13) = 1
    c: Equal(g13,g14)
    c: Equal(g13,g15)
    c: Equal(g13,g16)
    c: Coincident(g17,g0)
    c: InternalAlignment(g13-g16 -> g17) x4
    c: InternalAlignment(g18,g17)
    c: InternalAlignment(g19,g17)
    c: Block(g17)
FEATURE [Part::Extrusion] Extrude007  label="attatchmentPieceBottom003"
  Base = -> Sketch006
  Dir = (0,0,1)
  DirMode = 2
  FaceMakerClass = Part::FaceMakerBullseye
  LengthFwd = 3.2
  LengthRev = 0
  Placement = pos=(0,0,-6.5) rot=(0,0,1;0rad)
  Solid = true
  Symmetric = false
FEATURE [Part::Cut] Cut003  label="mainBumpperPieceAttatchment004"
  Base = -> Fillet006
  Placement = pos=(0,0,-3) rot=(0,0,1;0rad)
  Tool = -> Extrude005
FEATURE [Part::Chamfer] Chamfer
  Base = -> Extrude007
  Edges = 2 edges r=2.4: [Edge23,Edge26]
FEATURE [Part::Chamfer] Chamfer001  label="attatchmentPieceBottom004"
  Base = -> Chamfer
  Edges = 7 edges r=2.4: [Edge14,Edge15,Edge16,Edge17,Edge18,Edge19,Edge20]
FEATURE [Part::Fillet] Fillet007  label="attatchmentPieceBottom005"
  Base = -> Chamfer001
  Edges = 7 edges r=1.2: [Edge1,Edge2,Edge3,Edge4,Edge5,Edge6,Edge7]
FEATURE [Part::MultiFuse] Fusion007  label="attatchment"
  Shapes = -> [Fillet007,Fillet004,Fillet003,Fusion002,Extrude]
FEATURE [Part::Cylinder] Cylinder004  label="brace"
  Angle = 360
  AttacherType = Attacher::AttachEngine3D
  FirstAngle = 0
  Height = 32
  Placement = pos=(-42,0,0) rot=(0,1,0;1.5708rad)
  Radius = 2.4
  SecondAngle = 0
FEATURE [Part::Cylinder] Cylinder005  label="brace001"
  Angle = 360
  AttacherType = Attacher::AttachEngine3D
  FirstAngle = 0
  Height = 10
  Placement = pos=(29,0,0) rot=(0,1,0;1.5708rad)
  Radius = 2
  SecondAngle = 0
FEATURE [Part::Cylinder] Cylinder006  label="brace002"
  Angle = 360
  AttacherType = Attacher::AttachEngine3D
  FirstAngle = 0
  Height = 10
  Placement = pos=(-42,0,0) rot=(0,1,0;1.5708rad)
  Radius = 2
  SecondAngle = 0
FEATURE [Part::MultiFuse] Fusion008  label="leftBrace"
  Placement = pos=(-23,1.4,8) rot=(0,0,1;-0.785398rad)
  Shapes = -> [Cylinder004,Cylinder006]
FEATURE [Part::Cylinder] Cylinder007  label="brace003"
  Angle = 360
  AttacherType = Attacher::AttachEngine3D
  FirstAngle = 0
  Height = 32
  Placement = pos=(29,0,0) rot=(0,1,0;1.5708rad)
  Radius = 2.4
  SecondAngle = 0
FEATURE [Part::MultiFuse] Fusion009  label="rightBrace"
  Placement = pos=(6.4,-12,7) rot=(0,0,1;0.785398rad)
  Shapes = -> [Cylinder007,Cylinder005]
FEATURE [Part::Box] Box005  label="removeFromMainRight"
  AttacherType = Attacher::AttachEngine3D
  Height = 40
  Length = 44
  Placement = pos=(66,47,-6) rot=(0,0,1;-0.349066rad)
  Width = 20
FEATURE [Part::Box] Box006  label="removeFromMainLeft"
  AttacherType = Attacher::AttachEngine3D
  Height = 40
  Length = 44
  Placement = pos=(-110.35,31.95,-6) rot=(0,0,1;0.349066rad)
  Width = 20
FEATURE [Part::Cylinder] Cylinder008  label="brace004"
  Angle = 360
  AttacherType = Attacher::AttachEngine3D
  FirstAngle = 0
  Height = 32
  Placement = pos=(-42,0,0) rot=(0,1,0;1.5708rad)
  Radius = 2.4
  SecondAngle = 0
FEATURE [Part::Cylinder] Cylinder009  label="brace005"
  Angle = 360
  AttacherType = Attacher::AttachEngine3D
  FirstAngle = 0
  Height = 10
  Placement = pos=(-42,0,0) rot=(0,1,0;1.5708rad)
  Radius = 2
  SecondAngle = 0
FEATURE [Part::MultiFuse] Fusion010  label="leftBrace001"
  Placement = pos=(-23,1.4,-1) rot=(0,0,-1;0.785398rad)
  Shapes = -> [Cylinder008,Cylinder009]
FEATURE [Part::Cylinder] Cylinder010  label="brace006"
  Angle = 360
  AttacherType = Attacher::AttachEngine3D
  FirstAngle = 0
  Height = 10
  Placement = pos=(29,0,0) rot=(0,1,0;1.5708rad)
  Radius = 2
  SecondAngle = 0
FEATURE [Part::Cylinder] Cylinder011  label="brace007"
  Angle = 360
  AttacherType = Attacher::AttachEngine3D
  FirstAngle = 0
  Height = 32
  Placement = pos=(29,0,0) rot=(0,1,0;1.5708rad)
  Radius = 2.4
  SecondAngle = 0
FEATURE [Part::MultiFuse] Fusion011  label="rightBrace001"
  Placement = pos=(6.4,-12,-1) rot=(0,0,1;0.785398rad)
  Shapes = -> [Cylinder011,Cylinder010]
FEATURE [Part::Cylinder] Cylinder012  label="brace008"
  Angle = 360
  AttacherType = Attacher::AttachEngine3D
  FirstAngle = 0
  Height = 32
  Placement = pos=(-42,0,0) rot=(0,1,0;1.5708rad)
  Radius = 2.4
  SecondAngle = 0
FEATURE [Part::Cylinder] Cylinder013  label="brace009"
  Angle = 360
  AttacherType = Attacher::AttachEngine3D
  FirstAngle = 0
  Height = 10
  Placement = pos=(-42,0,0) rot=(0,1,0;1.5708rad)
  Radius = 2
  SecondAngle = 0
FEATURE [Part::MultiFuse] Fusion012  label="leftBrace002"
  Placement = pos=(-23,1.4,6) rot=(0,0,-1;0.785398rad)
  Shapes = -> [Cylinder012,Cylinder013]
FEATURE [Part::Cylinder] Cylinder014  label="brace010"
  Angle = 360
  AttacherType = Attacher::AttachEngine3D
  FirstAngle = 0
  Height = 10
  Placement = pos=(29,0,0) rot=(0,1,0;1.5708rad)
  Radius = 2
  SecondAngle = 0
FEATURE [Part::Cylinder] Cylinder015  label="brace011"
  Angle = 360
  AttacherType = Attacher::AttachEngine3D
  FirstAngle = 0
  Height = 32
  Placement = pos=(29,0,0) rot=(0,1,0;1.5708rad)
  Radius = 2.4
  SecondAngle = 0
FEATURE [Part::MultiFuse] Fusion013  label="rightBrace002"
  Placement = pos=(6.4,-12,5) rot=(0,0,1;0.785398rad)
  Shapes = -> [Cylinder015,Cylinder014]
FEATURE [Part::Cylinder] Cylinder016  label="brace012"
  Angle = 360
  AttacherType = Attacher::AttachEngine3D
  FirstAngle = 0
  Height = 10
  Placement = pos=(29,0,0) rot=(0,1,0;1.5708rad)
  Radius = 2
  SecondAngle = 0
FEATURE [Part::Cylinder] Cylinder017  label="brace013"
  Angle = 360
  AttacherType = Attacher::AttachEngine3D
  FirstAngle = 0
  Height = 32
  Placement = pos=(29,0,0) rot=(0,1,0;1.5708rad)
  Radius = 2.4
  SecondAngle = 0
FEATURE [Part::MultiFuse] Fusion014  label="rightBrace003"
  Placement = pos=(6.4,-12,2) rot=(0,0,1;0.785398rad)
  Shapes = -> [Cylinder017,Cylinder016]
FEATURE [Part::Cylinder] Cylinder018  label="brace014"
  Angle = 360
  AttacherType = Attacher::AttachEngine3D
  FirstAngle = 0
  Height = 32
  Placement = pos=(-42,0,0) rot=(0,1,0;1.5708rad)
  Radius = 2.4
  SecondAngle = 0
FEATURE [Part::Cylinder] Cylinder019  label="brace015"
  Angle = 360
  AttacherType = Attacher::AttachEngine3D
  FirstAngle = 0
  Height = 10
  Placement = pos=(-42,0,0) rot=(0,1,0;1.5708rad)
  Radius = 2
  SecondAngle = 0
FEATURE [Part::MultiFuse] Fusion015  label="leftBrace003"
  Placement = pos=(-23,1.4,2) rot=(0,0,-1;0.785398rad)
  Shapes = -> [Cylinder018,Cylinder019]
FEATURE [Part::Cut] Cut004
  Base = -> Extrude004
  Tool = -> Fusion001
FEATURE [Part::Cut] Cut005
  Base = -> Cut004
  Tool = -> Box006
FEATURE [Part::Cut] Cut006  label="main"
  Base = -> Cut005
  Tool = -> Box005
FEATURE [Part::Cylinder] Cylinder020  label="removeFromMain"
  Angle = 360
  AttacherType = Attacher::AttachEngine3D
  FirstAngle = 0
  Height = 40
  Placement = pos=(-1.5,39,-10) rot=(0,0,1;0rad)
  Radius = 4
  SecondAngle = 0
FEATURE [Part::Cylinder] Cylinder021  label="removeFromMain001"
  Angle = 360
  AttacherType = Attacher::AttachEngine3D
  FirstAngle = 0
  Height = 40
  Placement = pos=(-12.5,39,-10) rot=(0,0,1;0rad)
  Radius = 4
  SecondAngle = 0
FEATURE [Part::Cylinder] Cylinder022  label="removeFromMain002"
  Angle = 360
  AttacherType = Attacher::AttachEngine3D
  FirstAngle = 0
  Height = 40
  Placement = pos=(9.5,39,-10) rot=(0,0,1;0rad)
  Radius = 4
  SecondAngle = 0
FEATURE [Part::Cylinder] Cylinder023  label="removeFromMain003"
  Angle = 360
  AttacherType = Attacher::AttachEngine3D
  FirstAngle = 0
  Height = 40
  Placement = pos=(-34.5,39,-10) rot=(0,0,1;0rad)
  Radius = 4
  SecondAngle = 0
FEATURE [Part::Cylinder] Cylinder024  label="removeFromMain004"
  Angle = 360
  AttacherType = Attacher::AttachEngine3D
  FirstAngle = 0
  Height = 40
  Placement = pos=(31.5,39,-10) rot=(0,0,1;0rad)
  Radius = 4
  SecondAngle = 0
FEATURE [Part::Cylinder] Cylinder025  label="removeFromMain005"
  Angle = 360
  AttacherType = Attacher::AttachEngine3D
  FirstAngle = 0
  Height = 40
  Placement = pos=(-63.5,39,-10) rot=(0,0,1;0rad)
  Radius = 4
  SecondAngle = 0
FEATURE [Part::Cylinder] Cylinder026  label="removeFromMain006"
  Angle = 360
  AttacherType = Attacher::AttachEngine3D
  FirstAngle = 0
  Height = 40
  Placement = pos=(60.5,39,-10) rot=(0,0,1;0rad)
  Radius = 4
  SecondAngle = 0
FEATURE [Part::Cylinder] Cylinder027  label="removeFromMain007"
  Angle = 360
  AttacherType = Attacher::AttachEngine3D
  FirstAngle = 0
  Height = 40
  Placement = pos=(-74.5,38,-10) rot=(0,0,1;0rad)
  Radius = 4
  SecondAngle = 0
FEATURE [Part::Cylinder] Cylinder028  label="removeFromMain008"
  Angle = 360
  AttacherType = Attacher::AttachEngine3D
  FirstAngle = 0
  Height = 40
  Placement = pos=(71.5,38,-10) rot=(0,0,1;0rad)
  Radius = 4
  SecondAngle = 0
FEATURE [Part::MultiFuse] Fusion016  label="removeFromMain009"
  Shapes = -> [Cylinder020,Cylinder021,Cylinder022,Cylinder023,Cylinder024,Cylinder025,Cylinder026,Cylinder027,Cylinder028]
FEATURE [Part::Cut] Cut007
  Base = -> Cut006
  Tool = -> Fusion016
FEATURE [Sketcher::SketchObject] Sketch007  label="mainBumpperPieceAttatchmentBottomTop"
  FullyConstrained = false
  sketch-geometry (14):
    g0: Circle CenterX=28.85 CenterY=4.3 CenterZ=0 NormalX=0 NormalY=0 NormalZ=1 AngleXU=0 Radius=1
    g1: Circle CenterX=28.85 CenterY=11.9 CenterZ=0 NormalX=0 NormalY=0 NormalZ=1 AngleXU=0 Radius=1
    g2: Circle CenterX=21.05 CenterY=11.9 CenterZ=0 NormalX=0 NormalY=0 NormalZ=1 AngleXU=0 Radius=1
    g3: BSplineCurve PolesCount=3 KnotsCount=2 Degree=2 IsPeriodic=0
    g4: GeomPoint X=28.85 Y=4.3 Z=0
    g5: GeomPoint X=21.05 Y=11.9 Z=0
    g6: LineSegment StartX=-21.05 StartY=11.9 StartZ=0 EndX=21.05 EndY=11.9 EndZ=0
    g7: LineSegment StartX=28.85 StartY=4.3 StartZ=0 EndX=28.85 EndY=-4.3 EndZ=0
    g8: LineSegment StartX=28.85 StartY=-4.3 StartZ=0 EndX=28.85 EndY=-7.9 EndZ=0
    g9: BSplineCurve PolesCount=3 KnotsCount=2 Degree=2 IsPeriodic=0
    g10: LineSegment StartX=-31.95 StartY=-4.3 StartZ=0 EndX=-31.95 EndY=-7.9 EndZ=0
    g11: LineSegment StartX=-31.95 StartY=4.3 StartZ=0 EndX=-31.95 EndY=-4.3 EndZ=0
    g12: LineSegment StartX=-21.05 StartY=11.9 StartZ=0 EndX=-24.15 EndY=11.9 EndZ=0
    g13: LineSegment StartX=-31.95 StartY=-7.9 StartZ=0 EndX=28.85 EndY=-7.9 EndZ=0
  constraints (26):
    c: Weight(g0) = 1
    c: Equal(g0,g1)
    c: Equal(g0,g2)
    c: InternalAlignment(g0,g3)
    c: InternalAlignment(g1,g3)
    c: InternalAlignment(g2,g3)
    c: InternalAlignment(g4,g3)
    c: InternalAlignment(g5,g3)
    c: Block(g3)
    c: Horizontal(g6)
    c: Vertical(g7)
    c: Block(g7)
    c: Block(g6)
    c: Coincident(g8,g7)
    c: Vertical(g8)
    c: Distance(g8) = 3.6
    c: Block(g9)
    c: Vertical(g11)
    c: Block(g11)
    c: Vertical(g10)
    c: Coincident(g10,g11)
    c: Horizontal(g12)
    c: Coincident(g12,g6)
    c: Coincident(g13,g10)
    c: Coincident(g13,g8)
    c: Horizontal(g13)
FEATURE [Part::Extrusion] Extrude008  label="tob"
  Base = -> Sketch007
  Dir = (0,0,1)
  DirMode = 2
  FaceMakerClass = Part::FaceMakerBullseye
  LengthFwd = 2.4
  LengthRev = 0
  Placement = pos=(0,0,11) rot=(0,0,1;0rad)
  Solid = true
  Symmetric = false
FEATURE [Part::Extrusion] Extrude009  label="bottom"
  Base = -> Sketch007
  Dir = (0,0,1)
  DirMode = 2
  FaceMakerClass = Part::FaceMakerBullseye
  LengthFwd = 2.4
  LengthRev = 0
  Placement = pos=(0,0,-9.2) rot=(0,0,1;0rad)
  Solid = true
  Symmetric = false
FEATURE [Part::Box] Box007  label="attatchmentPieceSurroundBump003"
  AttacherType = Attacher::AttachEngine3D
  Height = 9.2
  Length = 7.2
  Placement = pos=(8.85,8.9,-1.4) rot=(0,0,1;0rad)
  Width = 1.3
FEATURE [Part::Box] Box008  label="attatchmentPieceSurroundBump004"
  AttacherType = Attacher::AttachEngine3D
  Height = 9.2
  Length = 7.2
  Placement = pos=(-19.15,8.9,-1.4) rot=(0,0,1;0rad)
  Width = 1.3
FEATURE [Part::MultiFuse] Fusion017  label="attatchmentPieceSurroundBump005"
  Placement = pos=(0,-0.4,0) rot=(0,0,1;0rad)
  Shapes = -> [Box008,Box007]
FEATURE [Sketcher::SketchObject] Sketch008  label="attatchmentPiece003"
  FullyConstrained = true
  sketch-geometry (20):
    g0: LineSegment StartX=21.05 StartY=0 StartZ=0 EndX=21.05 EndY=-1 EndZ=0
    g1: LineSegment StartX=21.05 StartY=-1 StartZ=0 EndX=21.05 EndY=-4.3 EndZ=0
    g2: LineSegment StartX=-24.15 StartY=4.3 StartZ=0 EndX=21.05 EndY=4.3 EndZ=0
    g3: LineSegment StartX=21.05 StartY=0 StartZ=0 EndX=21.05 EndY=4.3 EndZ=0
    g4-g7: Circle x4 (B-spline internal-alignment scaffolding for g8; pole/knot coordinates omitted)
    g8: BSplineCurve PolesCount=4 KnotsCount=2 Degree=3 IsPeriodic=0
    g9: GeomPoint X=10.05 Y=-1 Z=0
    g10: GeomPoint X=14.55 Y=-4.3 Z=0
    g11: LineSegment StartX=10.05 StartY=-1 StartZ=0 EndX=-10.05 EndY=-1 EndZ=0
    g12: LineSegment StartX=14.55 StartY=-4.3 StartZ=0 EndX=21.05 EndY=-4.3 EndZ=0
    g13: LineSegment StartX=-24.15 StartY=4.3 StartZ=0 EndX=-24.15 EndY=-4.3 EndZ=0
    g14: LineSegment StartX=-13.15 StartY=-1 StartZ=0 EndX=-10.05 EndY=-1 EndZ=0
    g15: LineSegment StartX=-24.15 StartY=-4.3 StartZ=0 EndX=-19.35 EndY=-4.3 EndZ=0
    g16: LineSegment StartX=-19.35 StartY=-4.3 StartZ=0 EndX=-17.65 EndY=-4.3 EndZ=0
    g17: BSplineCurve PolesCount=4 KnotsCount=2 Degree=3 IsPeriodic=0
    g18: Circle CenterX=16.25 CenterY=0 CenterZ=0 NormalX=0 NormalY=0 NormalZ=1 AngleXU=0 Radius=1.4
    g19: Circle CenterX=-19.35 CenterY=0 CenterZ=0 NormalX=0 NormalY=0 NormalZ=1 AngleXU=0 Radius=1.4
  constraints (41):
    c: Vertical(g0)
    c: Coincident(g1,g0)
    c: Vertical(g1)
    c: Block(g0)
    c: Horizontal(g2)
    c: Vertical(g3)
    c: Coincident(g3,g2)
    c: Block(g2)
    c: Block(g3)
    c: Weight(g4) = 1
    c: Equal(g4,g5)
    c: Equal(g4,g6)
    c: Equal(g4,g7)
    c: InternalAlignment(g4-g7 -> g8) x4
    c: InternalAlignment(g9,g8)
    c: InternalAlignment(g10,g8)
    c: Block(g8)
    c: Coincident(g11,g8)
    c: Horizontal(g11)
    c: Coincident(g12,g8)
    c: Coincident(g12,g1)
    c: Horizontal(g12)
    c: Distance(g2) = 45.2
    c: Coincident(g13,g2)
    c: Vertical(g13)
    c: Horizontal(g14)
    c: Distance(g14) = 3.1
    c: Horizontal(g15)
    c: Block(g17)
    c: Coincident(g16,g15)
    c: Coincident(g16,g17)
    c: Horizontal(g16)
    c: Block(g16)
    c: Coincident(g17,g14)
    c: Block(g15)
    c: Block(g11)
    c: Block(g13)
    c: Distance(g15) = 4.8
    c: Distance(g16) = 1.7
    c: Block(g18)
    c: Block(g19)
FEATURE [Part::Extrusion] Extrude010  label="attatchmentPiece002"
  Base = -> Sketch008
  Dir = (0,0,1)
  DirMode = 2
  FaceMakerClass = Part::FaceMakerBullseye
  LengthFwd = 7
  LengthRev = 0
  Solid = true
  Symmetric = false
FEATURE [Sketcher::SketchObject] Sketch009  label="attatchmentPieceSurround005"
  FullyConstrained = true
  sketch-geometry (18):
    g0: LineSegment StartX=25.85 StartY=-4.3 StartZ=0 EndX=21.05 EndY=-4.3 EndZ=0
    g1: LineSegment StartX=25.85 StartY=-4.3 StartZ=0 EndX=25.85 EndY=4.3 EndZ=0
    g2: LineSegment StartX=-21.05 StartY=8.9 StartZ=0 EndX=21.05 EndY=8.9 EndZ=0
    g3: Circle CenterX=21.05 CenterY=8.9 CenterZ=0 NormalX=0 NormalY=0 NormalZ=1 AngleXU=0 Radius=1
    g4: Circle CenterX=25.85 CenterY=8.9 CenterZ=0 NormalX=0 NormalY=0 NormalZ=1 AngleXU=0 Radius=1
    g5: Circle CenterX=25.85 CenterY=4.3 CenterZ=0 NormalX=0 NormalY=0 NormalZ=1 AngleXU=0 Radius=1
    g6: BSplineCurve PolesCount=3 KnotsCount=2 Degree=2 IsPeriodic=0
    g7: GeomPoint X=21.05 Y=8.9 Z=0
    g8: GeomPoint X=25.85 Y=4.3 Z=0
    g9: ArcOfCircle CenterX=19.45 CenterY=2.7 CenterZ=0 NormalX=0 NormalY=0 NormalZ=1 AngleXU=0 Radius=1.6 StartAngle=0 EndAngle=1.5708
    g10: LineSegment StartX=21.05 StartY=2.7 StartZ=0 EndX=21.05 EndY=-4.3 EndZ=0
    g11: BSplineCurve PolesCount=3 KnotsCount=2 Degree=2 IsPeriodic=0
    g12: LineSegment StartX=-28.95 StartY=-4.3 StartZ=0 EndX=-28.95 EndY=4.3 EndZ=0
    g13: LineSegment StartX=-24.15 StartY=-4.3 StartZ=0 EndX=-28.95 EndY=-4.3 EndZ=0
    g14: LineSegment StartX=-24.15 StartY=2.7 StartZ=0 EndX=-24.15 EndY=-4.3 EndZ=0
    g15: ArcOfCircle CenterX=-22.55 CenterY=2.7 CenterZ=0 NormalX=0 NormalY=0 NormalZ=1 AngleXU=0 Radius=1.6 StartAngle=1.5708 EndAngle=3.14159
    g16: LineSegment StartX=-24.15 StartY=8.9 StartZ=0 EndX=-21.05 EndY=8.9 EndZ=0
    g17: LineSegment StartX=-22.55 StartY=4.3 StartZ=0 EndX=19.45 EndY=4.3 EndZ=0
  constraints (38):
    c: Horizontal(g0)
    c: Vertical(g1)
    c: Coincident(g1,g0)
    c: Horizontal(g2)
    c: Distance(g2) = 42.1
    c: Block(g2)
    c: Coincident(g6,g2)
    c: Weight(g3) = 1
    c: Equal(g3,g4)
    c: Equal(g3,g5)
    c: Coincident(g6,g1)
    c: InternalAlignment(g3,g6)
    c: InternalAlignment(g4,g6)
    c: InternalAlignment(g5,g6)
    c: InternalAlignment(g7,g6)
    c: InternalAlignment(g8,g6)
    c: Block(g0)
    c: Block(g6)
    c: Block(g9)
    c: Coincident(g10,g9)
    c: Coincident(g10,g0)
    c: Vertical(g10)
    c: Horizontal(g13)
    c: Coincident(g12,g13)
    c: Vertical(g12)
    c: Coincident(g11,g12)
    c: Block(g12)
    c: Block(g11)
    c: Block(g15)
    c: Coincident(g14,g15)
    c: Coincident(g14,g13)
    c: Vertical(g14)
    c: Coincident(g16,g11)
    c: Coincident(g16,g2)
    c: Horizontal(g16)
    c: Coincident(g17,g15)
    c: Coincident(g17,g9)
    c: Horizontal(g17)
FEATURE [Part::Extrusion] Extrude011  label="attatchmentPieceSurround003"
  Base = -> Sketch009
  Dir = (0,0,1)
  DirMode = 2
  FaceMakerClass = Part::FaceMakerBullseye
  LengthFwd = 14.7
  LengthRev = 0
  Placement = pos=(0,0,-4.1) rot=(0,0,1;0rad)
  Solid = true
  Symmetric = false
FEATURE [Part::Fillet] Fillet009  label="attatchmentPieceSurround004"
  Base = -> Extrude011
  Edges = 3 edges r=1.2: [Edge19,Edge25,Edge31]
FEATURE [Sketcher::SketchObject] Sketch010  label="attatchmentPieceEndScrewHoleCaps005"
  FullyConstrained = true
  sketch-geometry (10):
    g0: ArcOfCircle CenterX=16.25 CenterY=0 CenterZ=0 NormalX=0 NormalY=0 NormalZ=1 AngleXU=0 Radius=4.3 StartAngle=2.05456 EndAngle=5.79942
    g1: LineSegment StartX=14.25 StartY=3.80657 StartZ=0 EndX=14.25 EndY=6 EndZ=0
    g2: LineSegment StartX=20.0566 StartY=-2 StartZ=0 EndX=22.25 EndY=-2 EndZ=0
    g3: LineSegment StartX=22.25 StartY=-2 StartZ=0 EndX=22.25 EndY=6 EndZ=0
    g4: LineSegment StartX=14.25 StartY=6 StartZ=0 EndX=22.25 EndY=6 EndZ=0
    g5: LineSegment StartX=-25.35 StartY=-2 StartZ=0 EndX=-25.35 EndY=6 EndZ=0
    g6: LineSegment StartX=-25.35 StartY=-2 StartZ=0 EndX=-23.1566 EndY=-2 EndZ=0
    g7: LineSegment StartX=-17.35 StartY=6 StartZ=0 EndX=-25.35 EndY=6 EndZ=0
    g8: LineSegment StartX=-17.35 StartY=3.80657 StartZ=0 EndX=-17.35 EndY=6 EndZ=0
    g9: ArcOfCircle CenterX=-19.35 CenterY=0 CenterZ=0 NormalX=0 NormalY=0 NormalZ=1 AngleXU=0 Radius=4.3 StartAngle=3.62536 EndAngle=7.37022
  constraints (25):
    c: Block(g0)
    c: Vertical(g1)
    c: Horizontal(g2)
    c: Coincident(g3,g2)
    c: Vertical(g3)
    c: Coincident(g4,g1)
    c: Horizontal(g4)
    c: Coincident(g3,g4)
    c: Block(g4)
    c: Block(g3)
    c: Coincident(g0,g1)
    c: Coincident(g0,g2)
    c: Block(g1)
    c: Block(g9)
    c: Horizontal(g6)
    c: Vertical(g8)
    c: Coincident(g7,g8)
    c: Horizontal(g7)
    c: Coincident(g5,g6)
    c: Vertical(g5)
    c: Coincident(g5,g7)
    c: Block(g7)
    c: Block(g5)
    c: Coincident(g9,g6)
    c: Coincident(g9,g8)
FEATURE [Part::Extrusion] Extrude012  label="attatchmentPieceEndScrewHoleCaps003"
  Base = -> Sketch010
  Dir = (0,0,1)
  DirMode = 2
  FaceMakerClass = Part::FaceMakerBullseye
  LengthFwd = 3.6
  LengthRev = 0
  Placement = pos=(0,0,7) rot=(0,0,1;0rad)
  Solid = true
  Symmetric = false
FEATURE [Part::Fillet] Fillet008  label="attatchmentPieceEndScrewHoleCaps004"
  Base = -> Extrude012
  Edges = 6 edges r=2.4: [Edge4,Edge7,Edge15,Edge25,Edge28,Edge30]
FEATURE [Sketcher::SketchObject] Sketch011  label="attatchmentPieceBottom009"
  FullyConstrained = true
  sketch-geometry (20):
    g0: LineSegment StartX=25.85 StartY=-4.3 StartZ=0 EndX=25.85 EndY=4.3 EndZ=0
    g1: LineSegment StartX=-21.05 StartY=8.9 StartZ=0 EndX=21.05 EndY=8.9 EndZ=0
    g2: Circle CenterX=21.05 CenterY=8.9 CenterZ=0 NormalX=0 NormalY=0 NormalZ=1 AngleXU=0 Radius=1
    g3: Circle CenterX=25.85 CenterY=8.9 CenterZ=0 NormalX=0 NormalY=0 NormalZ=1 AngleXU=0 Radius=1
    g4: Circle CenterX=25.85 CenterY=4.3 CenterZ=0 NormalX=0 NormalY=0 NormalZ=1 AngleXU=0 Radius=1
    g5: BSplineCurve PolesCount=3 KnotsCount=2 Degree=2 IsPeriodic=0
    g6: GeomPoint X=21.05 Y=8.9 Z=0
    g7: GeomPoint X=25.85 Y=4.3 Z=0
    g8: BSplineCurve PolesCount=3 KnotsCount=2 Degree=2 IsPeriodic=0
    g9: LineSegment StartX=-28.95 StartY=-4.3 StartZ=0 EndX=-28.95 EndY=4.3 EndZ=0
    g10: LineSegment StartX=-24.15 StartY=8.9 StartZ=0 EndX=-21.05 EndY=8.9 EndZ=0
    g11: Circle CenterX=-19.41 CenterY=0 CenterZ=0 NormalX=0 NormalY=0 NormalZ=1 AngleXU=0 Radius=3
    g12: Circle CenterX=16.3103 CenterY=0 CenterZ=0 NormalX=0 NormalY=0 NormalZ=1 AngleXU=0 Radius=3
    g13-g16: Circle x4 (B-spline internal-alignment scaffolding for g17; pole/knot coordinates omitted)
    g17: BSplineCurve PolesCount=4 KnotsCount=2 Degree=3 IsPeriodic=0
    g18: GeomPoint X=-28.95 Y=-4.3 Z=0
    g19: GeomPoint X=25.85 Y=-4.3 Z=0
  constraints (36):
    c: Vertical(g0)
    c: Horizontal(g1)
    c: Distance(g1) = 42.1
    c: Block(g1)
    c: Coincident(g5,g1)
    c: Weight(g2) = 1
    c: Equal(g2,g3)
    c: Equal(g2,g4)
    c: Coincident(g5,g0)
    c: InternalAlignment(g2,g5)
    c: InternalAlignment(g3,g5)
    c: InternalAlignment(g4,g5)
    c: InternalAlignment(g6,g5)
    c: InternalAlignment(g7,g5)
    c: Block(g5)
    c: Vertical(g9)
    c: Coincident(g8,g9)
    c: Block(g9)
    c: Block(g8)
    c: Coincident(g10,g8)
    c: Coincident(g10,g1)
    c: Horizontal(g10)
    c: PointOnObject(g12,g-1)
    c: PointOnObject(g11,g-1)
    c: Block(g11)
    c: Block(g12)
    c: Coincident(g17,g9)
    c: Weight(g13) = 1
    c: Equal(g13,g14)
    c: Equal(g13,g15)
    c: Equal(g13,g16)
    c: Coincident(g17,g0)
    c: InternalAlignment(g13-g16 -> g17) x4
    c: InternalAlignment(g18,g17)
    c: InternalAlignment(g19,g17)
    c: Block(g17)
FEATURE [Part::Extrusion] Extrude013  label="attatchmentPieceBottom007"
  Base = -> Sketch011
  Dir = (0,0,1)
  DirMode = 2
  FaceMakerClass = Part::FaceMakerBullseye
  LengthFwd = 3.2
  LengthRev = 0
  Placement = pos=(0,0,-6.5) rot=(0,0,1;0rad)
  Solid = true
  Symmetric = false
FEATURE [Part::Chamfer] Chamfer002
  Base = -> Extrude013
  Edges = 2 edges r=2.4: [Edge23,Edge26]
FEATURE [Part::Chamfer] Chamfer003  label="attatchmentPieceBottom006"
  Base = -> Chamfer002
  Edges = 7 edges r=2.4: [Edge14,Edge15,Edge16,Edge17,Edge18,Edge19,Edge20]
FEATURE [Part::Fillet] Fillet010  label="attatchmentPieceBottom008"
  Base = -> Chamfer003
  Edges = 7 edges r=1.2: [Edge1,Edge2,Edge3,Edge4,Edge5,Edge6,Edge7]
FEATURE [Part::MultiFuse] Fusion018  label="attatchment001"
  Shapes = -> [Fillet010,Fillet009,Fillet008,Fusion017,Extrude010]
FEATURE [Part::Cut] Cut008
  Base = -> Cut003
  Tool = -> Fusion007
